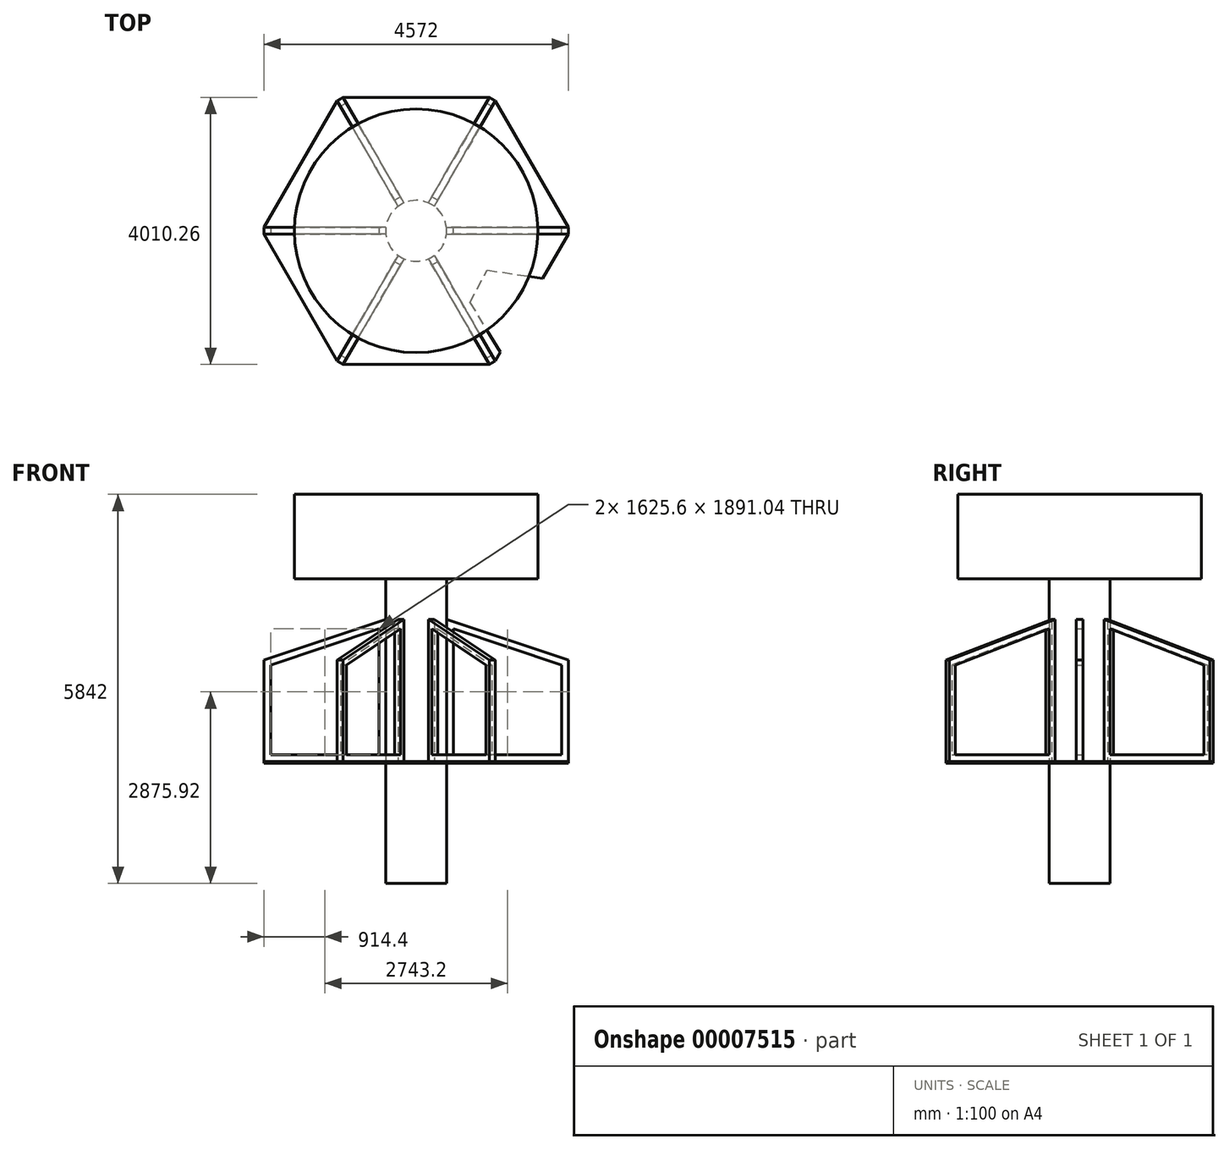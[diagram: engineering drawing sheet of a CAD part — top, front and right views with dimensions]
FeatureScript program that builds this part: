
annotation { "Feature Type Name" : "Feature", "Feature Type Description" : "" }
export const myFeature = defineFeature(function(context is Context, id is Id, definition is map)
    precondition{}
    {
        {
            var Q0;
            Q0=qCreatedBy(makeId("Front.planeOp"),FACE);
            var sketch = newSketch(context, id + "F0", { "sketchPlane" : qUnion([Q0])});
            skLineSegment(sketch, "E0", {"start": v(0, 0) * mm, "end": v(0, 5842) * mm});
            skLineSegment(sketch, "E1", {"start": v(0, 5842) * mm, "end": v(1828.8, 5842) * mm});
            skLineSegment(sketch, "E2", {"start": v(1828.8, 5842) * mm, "end": v(1828.8, 4572) * mm});
            skLineSegment(sketch, "E3", {"start": v(1828.8, 4572) * mm, "end": v(457.2, 4572) * mm});
            skLineSegment(sketch, "E4", {"start": v(457.2, 4572) * mm, "end": v(457.2, 0) * mm});
            skLineSegment(sketch, "E5", {"start": v(457.2, 0) * mm, "end": v(0, 0) * mm});
            skLineSegment(sketch, "E6", {"start": v(457.2, 3962.4) * mm, "end": v(2286, 3352.8) * mm});
            skLineSegment(sketch, "E7", {"start": v(2286, 3352.8) * mm, "end": v(2286, 1828.8) * mm});
            skLineSegment(sketch, "E8", {"start": v(2286, 1828.8) * mm, "end": v(457.2, 1828.8) * mm});
            skLineSegment(sketch, "E9", {"start": v(457.2, 1828.8) * mm, "end": v(457.2, 3962.4) * mm});
            skLineSegment(sketch, "E10.0", {"start": v(558.8, 3821.44) * mm, "end": v(2184.4, 3279.57) * mm});
            skLineSegment(sketch, "E10.1", {"start": v(558.8, 1930.4) * mm, "end": v(558.8, 3821.44) * mm});
            skLineSegment(sketch, "E10.2", {"start": v(2184.4, 1930.4) * mm, "end": v(558.8, 1930.4) * mm});
            skLineSegment(sketch, "E10.3", {"start": v(2184.4, 3279.57) * mm, "end": v(2184.4, 1930.4) * mm});
            skLineSegment(sketch, "E11.bottom", {"start": v(2286, 1828.8) * mm, "end": v(2184.4, 1828.8) * mm});
            skLineSegment(sketch, "E11.top", {"start": v(2286, 0) * mm, "end": v(2184.4, 0) * mm});
            skLineSegment(sketch, "E11.left", {"start": v(2286, 1828.8) * mm, "end": v(2286, 0) * mm});
            skLineSegment(sketch, "E11.right", {"start": v(2184.4, 1828.8) * mm, "end": v(2184.4, 0) * mm});
            skSolve(sketch);
        }
        {
            var Q0;
            Q0=makeQuery(id+"F0.imprint","IMPRINT",FACE,{"disambiguationData":[TD([[makeQuery(id+"F0.imprint","IMPRINT",EDGE,{"derivedFrom":sQuery(id+"F0.wireOp",EDGE,"E0")}),-1.0]])]});
            var Q1;
            Q1=sQuery(id+"F0.wireOp",EDGE,"E0");
            var Q2;
            Q2=sQuery(id+"F0.wireOp",EDGE,"E4");
            var Q3;
            Q3=sQuery(id+"F0.wireOp",EDGE,"E3");
            var Q4;
            Q4=sQuery(id+"F0.wireOp",EDGE,"E2");
            var Q5;
            Q5=sQuery(id+"F0.wireOp",EDGE,"E1");
            var Q6;
            Q6=sQuery(id+"F0.wireOp",EDGE,"E5");
            var Q7;
            Q7=sQuery(id+"F0.wireOp",EDGE,"E0");
            revolve(context, id + "F1", {"entities" : qUnion([Q0]), "surfaceEntities" : qUnion([Q1, Q2, Q3, Q4, Q5, Q6]), "axis" : qUnion([Q7]), "revolveType" : RevolveType.FULL});
        }
        {
            var Q0;
            Q0=makeQuery(id+"F0.imprint","IMPRINT",FACE,{"disambiguationData":[TD([[makeQuery(id+"F0.imprint","IMPRINT",EDGE,{"derivedFrom":sQuery(id+"F0.wireOp",EDGE,"E6")}),-1.0]])]});
            var Q1;
            Q1=makeQuery(id+"F0.imprint","IMPRINT",FACE,{"disambiguationData":[TD([[makeQuery(id+"F0.imprint","IMPRINT",EDGE,{"derivedFrom":sQuery(id+"F0.wireOp",EDGE,"E11.bottom")}),1.0]])]});
            extrude(context, id + "F2", {"entities" : qUnion([Q0, Q1]), "endBound" : BoundingType.SYMMETRIC, "depth" : 101.6 * mm});
        }
        {
            var Q0;
            Q0=makeQuery(id+"F2.opExtrude","SWEPT_BODY",BODY,{"disambiguationData":[OSD([sQuery(id+"F0.wireOp",EDGE,"E6"),sQuery(id+"F0.wireOp",EDGE,"E7"),sQuery(id+"F0.wireOp",EDGE,"E8"),sQuery(id+"F0.wireOp",EDGE,"E9"),sQuery(id+"F0.wireOp",EDGE,"E10.0"),sQuery(id+"F0.wireOp",EDGE,"E10.1"),sQuery(id+"F0.wireOp",EDGE,"E10.2"),sQuery(id+"F0.wireOp",EDGE,"E10.3")])]});
            var Q1;
            Q1=makeQuery(id+"F1.opRevolve","SWEPT_FACE",FACE,{"disambiguationData":[OSD([sQuery(id+"F0.wireOp",EDGE,"E4"),sQuery(id+"F0.wireOp",EDGE,"E9")])]});
            circularPattern(context, id + "F3", {"entities" : qUnion([Q0]), "axis" : qUnion([Q1]), "angle" : 60 * degree, "instanceCount" : 6});
        }
        {
            var Q0;
            Q0=makeQuery(id+"F2.opExtrude","SWEPT_FACE",FACE,{"disambiguationData":[OSD([sQuery(id+"F0.wireOp",EDGE,"E8")])]});
            var sketch = newSketch(context, id + "F4", { "sketchPlane" : qUnion([Q0])});
            skLineSegment(sketch, "E12", {"start": v(2286, 50.8) * mm, "end": v(1187, 1954.33) * mm});
            skLineSegment(sketch, "E13", {"start": v(-1187, 1954.33) * mm, "end": v(-2286, 50.8) * mm});
            skLineSegment(sketch, "E14", {"start": v(2286, 50.8) * mm, "end": v(2286, -50.8) * mm});
            skLineSegment(sketch, "E15", {"start": v(1187, 1954.33) * mm, "end": v(1099, 2005.13) * mm});
            skLineSegment(sketch, "E16", {"start": v(1099, 2005.13) * mm, "end": v(-1099, 2005.13) * mm});
            skLineSegment(sketch, "E17", {"start": v(-1099, 2005.13) * mm, "end": v(-1187, 1954.33) * mm});
            skLineSegment(sketch, "E18", {"start": v(-2286, 50.8) * mm, "end": v(-2286, -50.8) * mm});
            skLineSegment(sketch, "E19", {"start": v(-2286, -50.8) * mm, "end": v(-1187, -1954.33) * mm});
            skLineSegment(sketch, "E20", {"start": v(-1187, -1954.33) * mm, "end": v(-1099, -2005.13) * mm});
            skLineSegment(sketch, "E21", {"start": v(-1099, -2005.13) * mm, "end": v(1099, -2005.13) * mm});
            skLineSegment(sketch, "E22", {"start": v(1099, -2005.13) * mm, "end": v(1187, -1954.33) * mm});
            skLineSegment(sketch, "E23", {"start": v(1187, -1954.33) * mm, "end": v(2286, -50.8) * mm});
            skLineSegment(sketch, "E24", {"start": v(808.28, 1077.45) * mm, "end": v(1263.92, 1821.1) * mm});
            skLineSegment(sketch, "E25", {"start": v(808.28, 1077.45) * mm, "end": v(1066.25, 588.99) * mm});
            skLineSegment(sketch, "E26", {"start": v(1066.25, 588.99) * mm, "end": v(1901.77, 716.3) * mm});
            skSolve(sketch);
        }
        {
            var Q0;
            {var subQ0=sQuery(id+"F0.wireOp",EDGE,"E8");Q0=makeQuery(id+"F4.imprint","IMPRINT",FACE,{"disambiguationData":[TD([[makeQuery(id+"F4.imprint","IMPRINT",EDGE,{"derivedFrom":makeQuery(id+"F2.opExtrude","CAP_EDGE",EDGE,{"disambiguationData":[OSD([subQ0])],"isStart":true})}),-1.0]])]});}
            var Q1;
            Q1=makeQuery(id+"F4.imprint","IMPRINT",FACE,{"disambiguationData":[TD([[makeQuery(id+"F4.imprint","IMPRINT",EDGE,{"derivedFrom":sQuery(id+"F4.wireOp",EDGE,"E13")}),1.0]])]});
            extrude(context, id + "F5", {"entities" : qUnion([Q0, Q1]), "depth" : 25.4 * mm});
        }
    });
